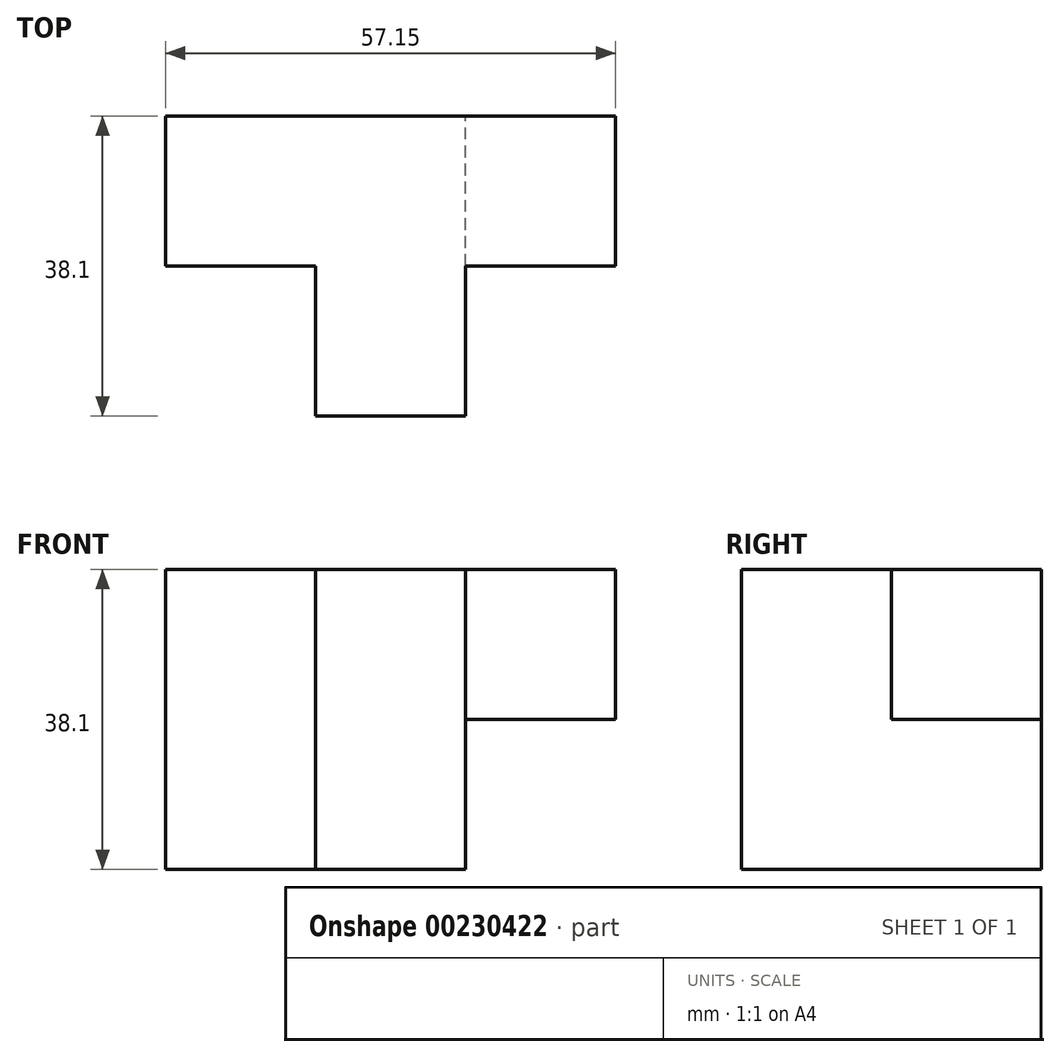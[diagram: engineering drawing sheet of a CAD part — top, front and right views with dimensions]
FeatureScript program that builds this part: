
annotation { "Feature Type Name" : "Feature", "Feature Type Description" : "" }
export const myFeature = defineFeature(function(context is Context, id is Id, definition is map)
    precondition{}
    {
        {
            var Q0;
            Q0=qCreatedBy(makeId("Front.planeOp"),FACE);
            var sketch = newSketch(context, id + "F0", { "sketchPlane" : qUnion([Q0])});
            skLineSegment(sketch, "E0.bottom", {"start": v(-97.43, 44.95) * mm, "end": v(-40.28, 44.95) * mm});
            skLineSegment(sketch, "E0.top", {"start": v(-97.43, 25.9) * mm, "end": v(-40.28, 25.9) * mm});
            skLineSegment(sketch, "E0.left", {"start": v(-97.43, 44.95) * mm, "end": v(-97.43, 25.9) * mm});
            skLineSegment(sketch, "E0.right", {"start": v(-40.28, 44.95) * mm, "end": v(-40.28, 25.9) * mm});
            skSolve(sketch);
        }
        {
            var Q0;
            Q0 = qSketchRegion(id + "F0", true);
            extrude(context, id + "F1", {"entities" : qUnion([Q0]), "depth" : 19.05 * mm});
        }
        {
            var Q0;
            Q0=makeQuery(id+"F1.opExtrude","CAP_FACE",FACE,{"disambiguationData":[OSD([sQuery(id+"F0.wireOp",EDGE,"E0.bottom"),sQuery(id+"F0.wireOp",EDGE,"E0.top"),sQuery(id+"F0.wireOp",EDGE,"E0.left"),sQuery(id+"F0.wireOp",EDGE,"E0.right")])],"isStart":false});
            var sketch = newSketch(context, id + "F2", { "sketchPlane" : qUnion([Q0])});
            skLineSegment(sketch, "E1.bottom", {"start": v(-78.38, 44.95) * mm, "end": v(-59.33, 44.95) * mm});
            skLineSegment(sketch, "E1.top", {"start": v(-78.38, 25.9) * mm, "end": v(-59.33, 25.9) * mm});
            skLineSegment(sketch, "E1.left", {"start": v(-78.38, 44.95) * mm, "end": v(-78.38, 25.9) * mm});
            skLineSegment(sketch, "E1.right", {"start": v(-59.33, 44.95) * mm, "end": v(-59.33, 25.9) * mm});
            skLineSegment(sketch, "E2.bottom", {"start": v(-59.33, 35.43) * mm, "end": v(-40.28, 35.43) * mm});
            skLineSegment(sketch, "E2.top", {"start": v(-59.33, 35.43) * mm, "end": v(-40.28, 35.43) * mm});
            skLineSegment(sketch, "E2.left", {"start": v(-59.33, 35.43) * mm, "end": v(-59.33, 35.43) * mm});
            skLineSegment(sketch, "E2.right", {"start": v(-40.28, 35.43) * mm, "end": v(-40.28, 35.43) * mm});
            skSolve(sketch);
        }
        {
            var Q0;
            Q0 = qSketchRegion(id + "F2", true);
            extrude(context, id + "F3", {"entities" : qUnion([Q0]), "operationType" : NewBodyOperationType.ADD, "depth" : 19.05 * mm});
        }
        {
            var Q0;
            Q0=makeQuery(id+"F3.boolean.opBoolean","MERGE",FACE,{"derivedFrom":[makeQuery(id+"F1.opExtrude","SWEPT_FACE",FACE,{"disambiguationData":[OSD([sQuery(id+"F0.wireOp",EDGE,"E0.top")])]}),makeQuery(id+"F3.opExtrude","SWEPT_FACE",FACE,{"disambiguationData":[OSD([sQuery(id+"F2.wireOp",EDGE,"E1.top")])]})]});
            var sketch = newSketch(context, id + "F4", { "sketchPlane" : qUnion([Q0])});
            skLineSegment(sketch, "E3.bottom", {"start": v(-97.43, 19.05) * mm, "end": v(-59.33, 19.05) * mm});
            skLineSegment(sketch, "E3.top", {"start": v(-97.43, 0) * mm, "end": v(-59.33, 0) * mm});
            skLineSegment(sketch, "E3.left", {"start": v(-97.43, 19.05) * mm, "end": v(-97.43, 0) * mm});
            skLineSegment(sketch, "E3.right", {"start": v(-59.33, 19.05) * mm, "end": v(-59.33, 0) * mm});
            skSolve(sketch);
        }
        {
            var Q0;
            Q0 = qSketchRegion(id + "F4", true);
            extrude(context, id + "F5", {"entities" : qUnion([Q0]), "operationType" : NewBodyOperationType.ADD, "depth" : 19.05 * mm});
        }
        {
            var Q0;
            {var subQ0=sQuery(id+"F2.wireOp",EDGE,"E1.top");var subQ1=makeQuery(id+"F3.opExtrude","SWEPT_FACE",FACE,{"disambiguationData":[OSD([subQ0])]});var subQ3=sQuery(id+"F2.wireOp",EDGE,"E1.left");var subQ4=sQuery(id+"F0.wireOp",EDGE,"E0.top");var subQ5=makeQuery(id+"F1.opExtrude","SWEPT_FACE",FACE,{"disambiguationData":[OSD([subQ4])]});Q0=makeQuery(id+"F5.boolean.opBoolean","SPLIT",FACE,{"disambiguationData":[TD([makeQuery(id+"F3.opExtrude","SWEPT_FACE",FACE,{"disambiguationData":[OSD([subQ3])]})])],"derivedFrom":makeQuery(id+"F3.boolean.opBoolean","MERGE",FACE,{"derivedFrom":[subQ5,subQ1]})});}
            var sketch = newSketch(context, id + "F6", { "sketchPlane" : qUnion([Q0])});
            skLineSegment(sketch, "E4.bottom", {"start": v(-78.38, 38.1) * mm, "end": v(-59.33, 38.1) * mm});
            skLineSegment(sketch, "E4.top", {"start": v(-78.38, 19.05) * mm, "end": v(-59.33, 19.05) * mm});
            skLineSegment(sketch, "E4.left", {"start": v(-78.38, 38.1) * mm, "end": v(-78.38, 19.05) * mm});
            skLineSegment(sketch, "E4.right", {"start": v(-59.33, 38.1) * mm, "end": v(-59.33, 19.05) * mm});
            skSolve(sketch);
        }
        {
            var Q0;
            Q0 = qSketchRegion(id + "F6", true);
            extrude(context, id + "F7", {"entities" : qUnion([Q0]), "operationType" : NewBodyOperationType.ADD, "depth" : 19.05 * mm});
        }
    });
